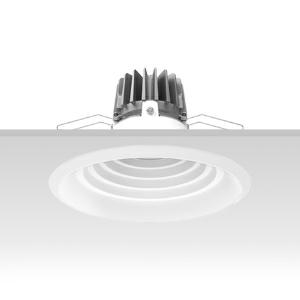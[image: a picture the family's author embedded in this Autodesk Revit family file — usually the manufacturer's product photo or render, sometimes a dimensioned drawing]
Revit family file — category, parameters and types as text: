
# Revit family: 3f_filippi_-_3f_reno_bianco_ugr_3f_filippi_-_30725_-_3f_reno_200_wh_2000-930_ugr
name_source: partatom
category: Lighting Fixtures
units: mm (PartAtom-declared; Revit-internal decimal feet)

## family parameters
Cut with Voids When Loaded = No
Host = Face
Light Source = No
Part Type = Normal
Room Calculation Point = No
Round Connector Dimension = Use Diameter
Shared = No

## types (1)
- 3F Filippi - 3F Reno Bianco UGR (1 x LED, 2354 lm, 24 W, 3000 K)
    Apparent Load = 24 VA
    Approval mark = CE
    CIE Flux Codes = 90 100 100 100 100
    Color Rendering = 90
    Color Temperature = 3000 K
    Control Gear = Electronic ballast
    Default Elevation = 1800 mm
    Description = ILLUMINOTECHNICAL
Luminous efficiency 100% (DLOR 100%, ULOR 0%).
Initial luminous flux of the luminaire 2354 lm.
Direct symmetric UGR distribution.
Installation Interdistance Transv.D = 0.99 x hu - Long.D = 1.01 x hu.
Average luminance <500 cd/m² for radial angles >65°.
Tabular UGR (CIE 117 - 4H-8H; S=0.25H; 70/50/20): RUG 17.2 - 17.2.
Beam angle: 64° - 65°.
Luminous efficacy 98 lm/W.
Lifetime (L90/B10): 30000 h. (tq+25°C)
Lifetime (L85/B10): 50000 h. (tq+25°C)
Lifetime (L70/B10): 80000 h. (tq+25°C)
Sudden decreased luminous flux after 50000 hours: 0% (C0).
Photobiological safety in compliance with IEC/TR 62778: RG0 risk exempt, (IEC 62471).
In compliance with IEC/EN 62722-2-1 - IEC/EN 62717 standards.

SOURCE
Compact LED module 2000/930.
Energy efficiency class (UE 2019/2020 - UE 2019/2015): E.
CIE 13.3 Colour rendering index: CRI >90 (R9 >50%).
IES TM-30 Fidelity Index: Rf = 92 Rg = 101.
CCT nominal colour temperature 3000 K.
Colour initial tolerance (MacAdam): SDCM 3.
Zhaga Book 3 compliant.

MECHANICAL
Passive heat dissipator in die-casting aluminium, oversized, for optimum thermal management of the LED module.
Parabolic element with graduated/concentric rings in white polycarbonate.
Internal specular metallic louvre to optimise control of the luminous flux in polycarbonate.
Transparent external lens with glossy and satin differentiated surfaces, with a cooling and anti-insect system in methacrylate (PMMA).
Fastening spring clips in stainless steel.
Dimensions: diameter 216 mm, height 142 mm. Weight 0.82 kg.
IP44 protection degree for exposed part, IP20 for recessed part.
Mechanical strength to impacts IK04 (0.5 joule).
Glow-wire test resistance 650°C.

ELECTRICAL
Wiring on a separate unit.
Halogen Free electronic wiring 230V-50/60Hz, power factor 0.95, THD <25%, constant output current, SELV, class II, 1 driver.
Power of the luminaire 24 W.
ENEC - CE.
SAFE FLICKER: PstLM=<1 and SVM=<0.4 (IEC TR 61547-1 and IEC TR 63158), to ensure a more comfortable and safe light.
Luminaire compliant with EN 60598-2-22 for power supply from a centralised emergency system CPSS (Central Power Supply System), not incorporated in the luminaire - high risk areas excluded. The default power and flux are 100% in AC and 100% in DC.
Ambient temperature from 0°C to +25°C.
Temperature class T6 max 85°C.
Relative humidity UR: <85%.

INSTALLATION
Pull-up recessed fitting.
False ceiling carving: 200 mm.
All accessories dedicated to this product are available on the Catalog and on our website www.3F-Filippi.com.

APPLICATIONS
In environments with VDTs, managerial offices and staterooms, public offices and schools.
In false ceilings with narrow voids.

WARNING
Luminaire designed for disposal/recycling at end-of-life.
Replaceable (LED only) light source by a professional. Replaceable control gear by a professional.
    Height = 0 mm  [stored 0 ft]
    Lamp = 1 x LED
    Lamp Light Flux = 2354 lm
    Lamp Power = 24 W
    Lamp count = 1
    Length = 216 mm
    Lifetime = 50000 h
    Luminous efficacy = 98 lm/W
    Manufacturer = 3F Filippi
    ModVariant = No
    Model = 3F Filippi - 30725 - 3F Reno 200 WH 2000-930 UGR
    Mounting Place = Ceiling
    Mounting Type = Recessed
    Number of Poles = 1
    OnlyDefault = Yes
    Power Factor = 1
    Product Name = 3F Filippi - 3F Reno Bianco UGR
    Product group = recessed luminaire
    ProductGroupID = 4
    Protection Class = Protection class II
    Protection Degree = IP 20
    RLX_Detail_Level = 1
    RLX_Emergency_Light_Flux = 0 lm
    RLX_Emergency_Type = 0
    RLX_Emergency_Type_DB = No
    RlxData = <blob elided: 87385 chars, md5=284eddbc>
    Socket = socket
    Standby Power = 0 W
    System Light Flux = 2354 lm
    System Power = 24 W
    Type Comments = Product without accessories
    Type Image = 3ffilippi_3f_reno_200_wh_2000.jpg
    URL = http://relux.com
    VarID = ---
    Voltage = 0 V
    Weight = 0.00 kg
    Width = 0 mm  [stored 0 ft]

note: [stored X ft] marks values corroborated as IEEE doubles in the binary element streams (Revit-internal decimal feet)

## geometry (parser evidence)
native form markers: Blend x4, Sweep x10
no freeform markers — native parametric forms only
